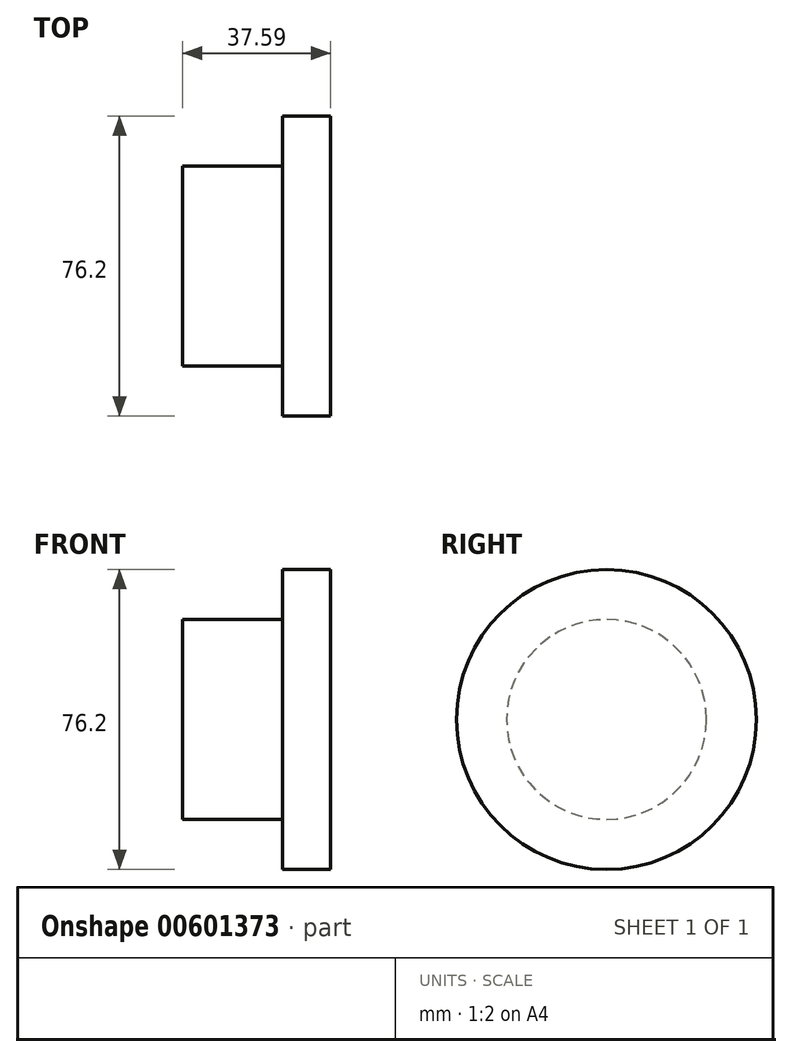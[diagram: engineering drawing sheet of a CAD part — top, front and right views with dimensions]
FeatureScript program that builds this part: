
annotation { "Feature Type Name" : "Feature", "Feature Type Description" : "" }
export const myFeature = defineFeature(function(context is Context, id is Id, definition is map)
    precondition{}
    {
        {
            var Q0;
            Q0=qCreatedBy(makeId("Right.planeOp"),FACE);
            var sketch = newSketch(context, id + "F0", { "sketchPlane" : qUnion([Q0])});
            skCircle(sketch, "E0", {"center": v(0, 0) * mm, "radius": 38.1 * mm});
            skCircle(sketch, "E1", {"center": v(0, 0) * mm, "radius": 25.4 * mm});
            skSolve(sketch);
        }
        {
            var Q0;
            Q0=makeQuery(id+"F0.imprint","IMPRINT",FACE,{"disambiguationData":[TD([[makeQuery(id+"F0.imprint","IMPRINT",EDGE,{"derivedFrom":sQuery(id+"F0.wireOp",EDGE,"E0")}),1.0]])]});
            var Q1;
            Q1=makeQuery(id+"F0.imprint","IMPRINT",FACE,{"disambiguationData":[TD([[makeQuery(id+"F0.imprint","IMPRINT",EDGE,{"derivedFrom":sQuery(id+"F0.wireOp",EDGE,"E1")}),1.0]])]});
            var Q2;
            Q2=sQuery(id+"F0.wireOp",EDGE,"E0");
            var Q3;
            Q3=sQuery(id+"F0.wireOp",EDGE,"E1");
            extrude(context, id + "F1", {"entities" : qUnion([Q0, Q1]), "surfaceEntities" : qUnion([Q2, Q3]), "depth" : 12.2 * mm, "offsetDistance" : 25.4 * mm});
        }
        {
            var Q0;
            Q0=makeQuery(id+"F0.imprint","IMPRINT",FACE,{"disambiguationData":[TD([[makeQuery(id+"F0.imprint","IMPRINT",EDGE,{"derivedFrom":sQuery(id+"F0.wireOp",EDGE,"E1")}),1.0]])]});
            extrude(context, id + "F2", {"entities" : qUnion([Q0]), "operationType" : NewBodyOperationType.ADD, "oppositeDirection" : true, "depth" : 25.4 * mm, "offsetDistance" : 25.4 * mm});
        }
    });
